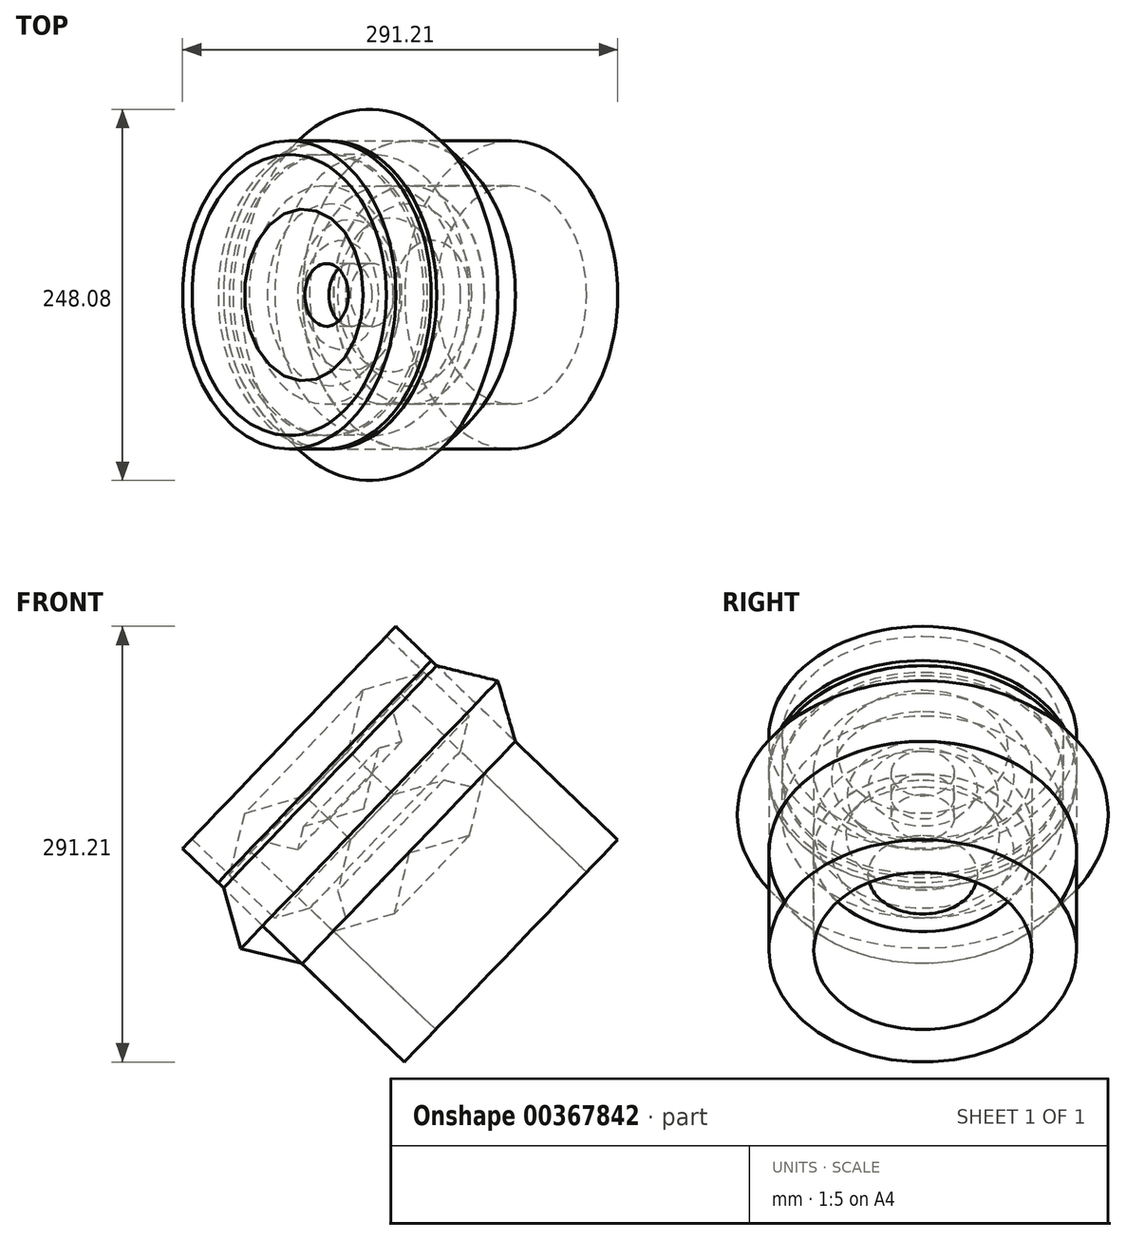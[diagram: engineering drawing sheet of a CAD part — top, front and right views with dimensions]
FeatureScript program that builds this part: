
annotation { "Feature Type Name" : "Feature", "Feature Type Description" : "" }
export const myFeature = defineFeature(function(context is Context, id is Id, definition is map)
    precondition{}
    {
        {
            var Q0;
            Q0=qCreatedBy(makeId("Front.planeOp"),FACE);
            var sketch = newSketch(context, id + "F0", { "sketchPlane" : qUnion([Q0])});
            skCircle(sketch, "E0.cCircle", {"center": v(-76.67, 47.12) * mm, "radius": 36.46 * mm, "construction": true});
            skLineSegment(sketch, "E0.0", {"start": v(-36.23, 58.83) * mm, "end": v(-46.31, 17.96) * mm});
            skLineSegment(sketch, "E0.1", {"start": v(-46.31, 17.96) * mm, "end": v(-86.74, 6.25) * mm});
            skLineSegment(sketch, "E0.2", {"start": v(-86.74, 6.25) * mm, "end": v(-117.1, 35.41) * mm});
            skLineSegment(sketch, "E0.3", {"start": v(-117.1, 35.41) * mm, "end": v(-107.02, 76.28) * mm});
            skLineSegment(sketch, "E0.4", {"start": v(-107.02, 76.28) * mm, "end": v(-66.6, 88) * mm});
            skLineSegment(sketch, "E0.5", {"start": v(-66.6, 88) * mm, "end": v(-36.23, 58.83) * mm});
            skPoint(sketch, "E0.0.midPoint", {"position": v(-41.27, 38.4) * mm});
            skCircle(sketch, "E1.cCircle", {"center": v(-116.05, 55.85) * mm, "radius": 36.46 * mm, "construction": true});
            skPoint(sketch, "E1.cCircle.centerSnap0", {"position": v(-112.06, 55.85) * mm});
            skLineSegment(sketch, "E1.0", {"start": v(-75.62, 67.56) * mm, "end": v(-85.7, 26.69) * mm});
            skLineSegment(sketch, "E1.1", {"start": v(-85.7, 26.69) * mm, "end": v(-126.13, 14.98) * mm});
            skLineSegment(sketch, "E1.2", {"start": v(-126.13, 14.98) * mm, "end": v(-156.48, 44.14) * mm});
            skLineSegment(sketch, "E1.3", {"start": v(-156.48, 44.14) * mm, "end": v(-146.4, 85.01) * mm});
            skLineSegment(sketch, "E1.4", {"start": v(-146.4, 85.01) * mm, "end": v(-105.97, 96.72) * mm});
            skLineSegment(sketch, "E1.5", {"start": v(-105.97, 96.72) * mm, "end": v(-75.62, 67.56) * mm});
            skPoint(sketch, "E1.0.midPoint", {"position": v(-80.66, 47.12) * mm});
            skCircle(sketch, "E2.cCircle", {"center": v(-119.54, 25.27) * mm, "radius": 36.48 * mm, "construction": true});
            skLineSegment(sketch, "E2.0", {"start": v(-78.64, 15.19) * mm, "end": v(-107.82, -15.19) * mm});
            skLineSegment(sketch, "E2.1", {"start": v(-107.82, -15.19) * mm, "end": v(-148.72, -5.1) * mm});
            skLineSegment(sketch, "E2.2", {"start": v(-148.72, -5.1) * mm, "end": v(-160.44, 35.36) * mm});
            skLineSegment(sketch, "E2.3", {"start": v(-160.44, 35.36) * mm, "end": v(-131.26, 65.74) * mm});
            skLineSegment(sketch, "E2.4", {"start": v(-131.26, 65.74) * mm, "end": v(-90.36, 55.65) * mm});
            skLineSegment(sketch, "E2.5", {"start": v(-90.36, 55.65) * mm, "end": v(-78.64, 15.19) * mm});
            skPoint(sketch, "E2.0.midPoint", {"position": v(-93.23, 0) * mm});
            skSolve(sketch);
        }
        {
            var Q0;
            {var subQ0=sQuery(id+"F0.wireOp",EDGE,"E2.1");Q0=makeQuery(id+"F0.imprint","IMPRINT",FACE,{"disambiguationData":[TD([[makeQuery(id+"F0.imprint","IMPRINT",EDGE,{"derivedFrom":subQ0}),-1.0]])]});}
            var Q1;
            {var subQ0=sQuery(id+"F0.wireOp",EDGE,"E1.3");Q1=makeQuery(id+"F0.imprint","IMPRINT",FACE,{"disambiguationData":[TD([[makeQuery(id+"F0.imprint","IMPRINT",EDGE,{"derivedFrom":subQ0}),-1.0]])]});}
            var Q2;
            Q2=makeQuery(id+"F0.imprint","IMPRINT",FACE,{"disambiguationData":[TD([[makeQuery(id+"F0.imprint","IMPRINT",EDGE,{"derivedFrom":sQuery(id+"F0.wireOp",EDGE,"E0.0")}),-1.0]])]});
            var Q3;
            Q3=sQuery(id+"F0.wireOp",EDGE,"E0.5");
            revolve(context, id + "F1", {"entities" : qUnion([Q0, Q1, Q2]), "axis" : qUnion([Q3]), "revolveType" : RevolveType.FULL});
        }
        {
            var Q0;
            {var subQ0=sQuery(id+"F0.wireOp",EDGE,"E2.3");Q0=makeQuery(id+"F1.opRevolve","SWEPT_FACE",FACE,{"disambiguationData":[OSD([subQ0]),TDD([makeQuery(id+"F0.imprint","IMPRINT",EDGE,{"disambiguationData":[TD([[makeQuery(id+"F0.imprint","INTERSECT",VERTEX,{"derivedFrom":[sQuery(id+"F0.wireOp",EDGE,"E2.2"),subQ0]}),-1.0]])],"derivedFrom":subQ0})])]});}
            extrude(context, id + "F2", {"entities" : qUnion([Q0]), "depth" : 38 * mm});
        }
        {
            var Q0;
            {var subQ0=sQuery(id+"F0.wireOp",EDGE,"E2.0");Q0=makeQuery(id+"F1.opRevolve","SWEPT_FACE",FACE,{"disambiguationData":[OSD([subQ0]),TDD([makeQuery(id+"F0.imprint","IMPRINT",EDGE,{"disambiguationData":[TD([[makeQuery(id+"F0.imprint","INTERSECT",VERTEX,{"derivedFrom":[subQ0,sQuery(id+"F0.wireOp",EDGE,"E2.1")]}),1.0]])],"derivedFrom":subQ0})])]});}
            extrude(context, id + "F3", {"entities" : qUnion([Q0]), "depth" : 95 * mm});
        }
        {
            var Q0;
            Q0=makeQuery(id+"F3.opExtrude","CAP_FACE",FACE,{"disambiguationData":[OSD([sQuery(id+"F0.wireOp",EDGE,"E2.0")])],"isStart":false});
            extrude(context, id + "F4", {"entities" : qUnion([Q0]), "oppositeDirection" : true, "depth" : 173 * mm});
        }
    });
